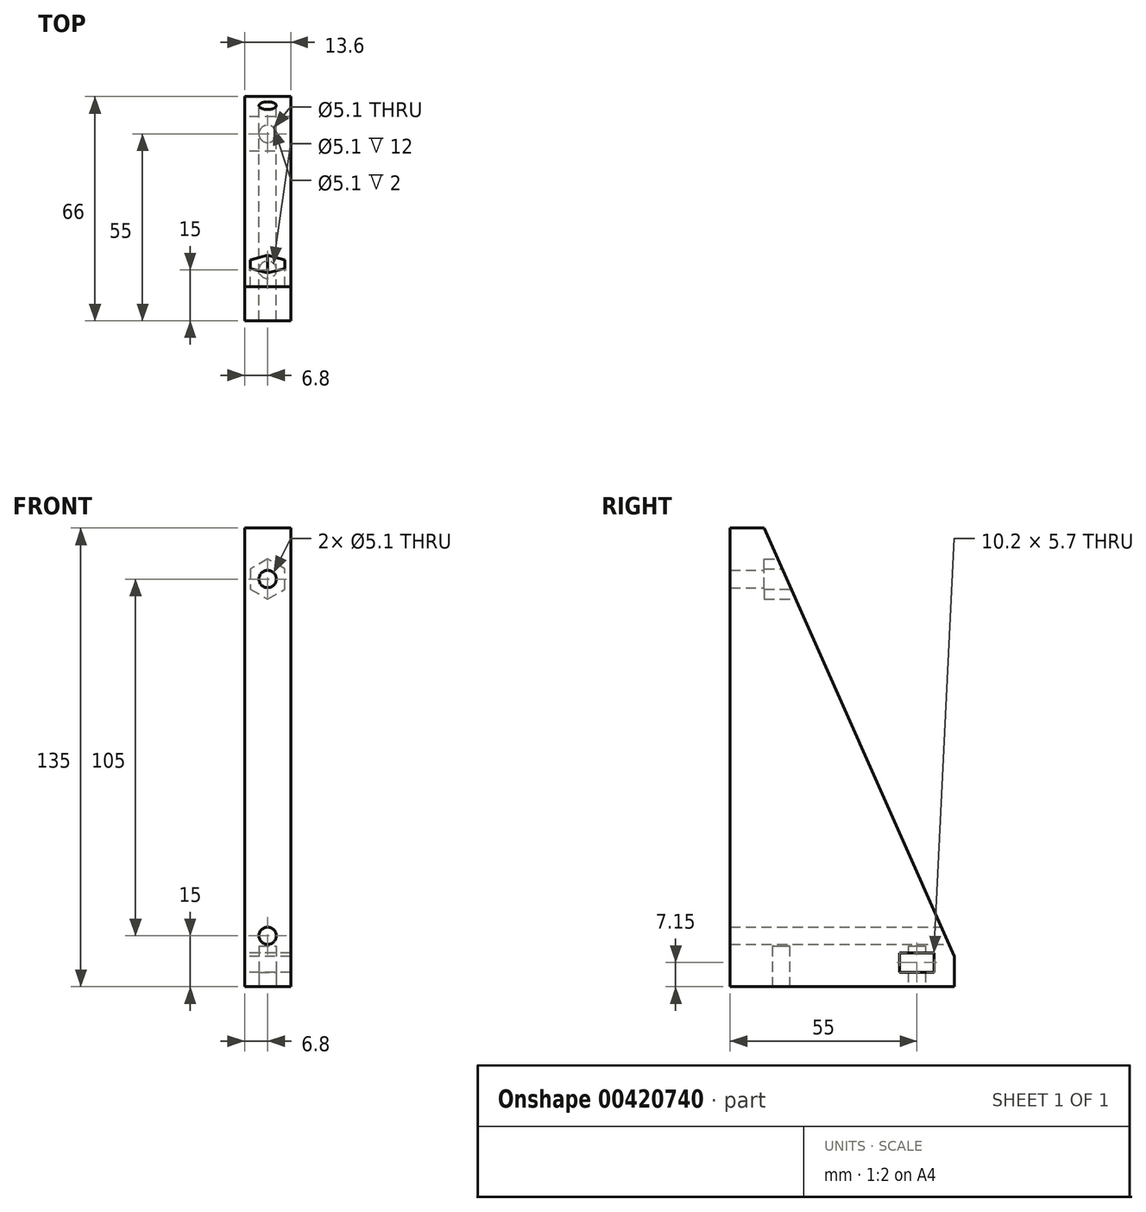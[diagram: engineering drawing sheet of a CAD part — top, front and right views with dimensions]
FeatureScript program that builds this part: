
annotation { "Feature Type Name" : "Feature", "Feature Type Description" : "" }
export const myFeature = defineFeature(function(context is Context, id is Id, definition is map)
    precondition{}
    {
        {
            var Q0;
            Q0=qCreatedBy(makeId("Right.planeOp"),FACE);
            var sketch = newSketch(context, id + "F0", { "sketchPlane" : qUnion([Q0])});
            skLineSegment(sketch, "E0", {"start": v(0, 0) * mm, "end": v(-70, 0) * mm});
            skLineSegment(sketch, "E1", {"start": v(-70, 0) * mm, "end": v(-70, 135) * mm});
            skLineSegment(sketch, "E2", {"start": v(-70, 135) * mm, "end": v(-60, 135) * mm});
            skLineSegment(sketch, "E3", {"start": v(-60, 135) * mm, "end": v(0, 0) * mm});
            skSolve(sketch);
        }
        {
            var Q0;
            Q0 = qSketchRegion(id + "F0", true);
            extrude(context, id + "F1", {"entities" : qUnion([Q0]), "depth" : 13.6 * mm});
        }
        {
            var Q0;
            Q0=makeQuery(id+"F1.opExtrude","SWEPT_FACE",FACE,{"disambiguationData":[OSD([sQuery(id+"F0.wireOp",EDGE,"E1")])]});
            var sketch = newSketch(context, id + "F2", { "sketchPlane" : qUnion([Q0])});
            skLineSegment(sketch, "E4", {"start": v(6.8, 135) * mm, "end": v(6.8, 120) * mm});
            skLineSegment(sketch, "E5", {"start": v(6.8, 0) * mm, "end": v(6.8, 15) * mm});
            skPoint(sketch, "E6.0.midPoint", {"position": v(16.6, 120) * mm});
            skCircle(sketch, "E7.cCircle", {"center": v(6.8, 15) * mm, "radius": 5.1 * mm, "construction": true});
            skLineSegment(sketch, "E7.0", {"start": v(1.7, 12.06) * mm, "end": v(1.7, 17.94) * mm});
            skLineSegment(sketch, "E7.1", {"start": v(1.7, 17.94) * mm, "end": v(6.8, 20.89) * mm});
            skLineSegment(sketch, "E7.2", {"start": v(6.8, 20.89) * mm, "end": v(11.9, 17.94) * mm});
            skLineSegment(sketch, "E7.3", {"start": v(11.9, 17.94) * mm, "end": v(11.9, 12.06) * mm});
            skLineSegment(sketch, "E7.4", {"start": v(11.9, 12.06) * mm, "end": v(6.8, 9.11) * mm});
            skLineSegment(sketch, "E7.5", {"start": v(6.8, 9.11) * mm, "end": v(1.7, 12.06) * mm});
            skPoint(sketch, "E7.0.midPoint", {"position": v(1.7, 15) * mm});
            skCircle(sketch, "E8.cCircle", {"center": v(6.8, 120) * mm, "radius": 5.1 * mm, "construction": true});
            skLineSegment(sketch, "E8.0", {"start": v(1.7, 117.06) * mm, "end": v(1.7, 122.94) * mm});
            skLineSegment(sketch, "E8.1", {"start": v(1.7, 122.94) * mm, "end": v(6.8, 125.89) * mm});
            skLineSegment(sketch, "E8.2", {"start": v(6.8, 125.89) * mm, "end": v(11.9, 122.94) * mm});
            skLineSegment(sketch, "E8.3", {"start": v(11.9, 122.94) * mm, "end": v(11.9, 117.06) * mm});
            skLineSegment(sketch, "E8.4", {"start": v(11.9, 117.06) * mm, "end": v(6.8, 114.11) * mm});
            skLineSegment(sketch, "E8.5", {"start": v(6.8, 114.11) * mm, "end": v(1.7, 117.06) * mm});
            skPoint(sketch, "E8.0.midPoint", {"position": v(1.7, 120) * mm});
            skSolve(sketch);
        }
        {
            var Q0;
            Q0=sQuery(id+"F2.wireOp",VERTEX,"E5.end");
            var Q1;
            Q1=sQuery(id+"F2.wireOp",VERTEX,"E4.end");
            var Q2;
            Q2=makeQuery(id+"F1.opExtrude","SWEPT_BODY",BODY,{"disambiguationData":[OSD([sQuery(id+"F0.wireOp",EDGE,"E0"),sQuery(id+"F0.wireOp",EDGE,"E1"),sQuery(id+"F0.wireOp",EDGE,"E2"),sQuery(id+"F0.wireOp",EDGE,"E3")])]});
            hole(context, id + "F3", {"style" : HoleStyle.SIMPLE, "endStyle" : HoleEndStyle.THROUGH, "holeDiameter" : 5.1 * mm, "isTappedThrough" : true, "tappedDepth" : 12 * mm, "tapClearance" : 3, "locations" : qUnion([Q0, Q1]), "scope" : qUnion([Q2]), "startStyle" : HoleStartStyle.PART});
        }
        {
            var Q0;
            Q0=makeQuery(id+"F1.opExtrude","SWEPT_FACE",FACE,{"disambiguationData":[OSD([sQuery(id+"F0.wireOp",EDGE,"E0")])]});
            var sketch = newSketch(context, id + "F4", { "sketchPlane" : qUnion([Q0])});
            skLineSegment(sketch, "E9", {"start": v(6.8, 70) * mm, "end": v(6.8, 55) * mm});
            skLineSegment(sketch, "E10", {"start": v(6.8, 55) * mm, "end": v(6.8, 15) * mm});
            skPoint(sketch, "E10.endSnap0", {"position": v(6.8, 0) * mm});
            skCircle(sketch, "E11", {"center": v(6.8, 55) * mm, "radius": 2.55 * mm});
            skCircle(sketch, "E12", {"center": v(6.8, 15) * mm, "radius": 2.55 * mm});
            skLineSegment(sketch, "E13", {"start": v(6.8, 0) * mm, "end": v(6.8, 4) * mm});
            skLineSegment(sketch, "E14", {"start": v(6.8, 4) * mm, "end": v(13.6, 4) * mm});
            skLineSegment(sketch, "E15", {"start": v(13.6, 4) * mm, "end": v(0, 4) * mm});
            skSolve(sketch);
        }
        {
            var Q0;
            Q0 = qSketchRegion(id + "F4", true);
            extrude(context, id + "F5", {"entities" : qUnion([Q0]), "operationType" : NewBodyOperationType.REMOVE, "oppositeDirection" : true, "depth" : 12 * mm});
        }
        {
            var Q0;
            Q0=makeQuery(id+"F2.imprint","IMPRINT",FACE,{"disambiguationData":[TD([[makeQuery(id+"F2.imprint","IMPRINT",EDGE,{"derivedFrom":sQuery(id+"F2.wireOp",EDGE,"E6.0")}),-1.0]])]});
            var Q1;
            Q1=makeQuery(id+"F2.imprint","IMPRINT",FACE,{"disambiguationData":[TD([[makeQuery(id+"F2.imprint","IMPRINT",EDGE,{"derivedFrom":sQuery(id+"F2.wireOp",EDGE,"E8.0")}),-1.0]])]});
            extrude(context, id + "F6", {"entities" : qUnion([Q0, Q1]), "operationType" : NewBodyOperationType.ADD, "oppositeDirection" : true, "depth" : 25 * mm});
        }
        {
            var Q0;
            Q0=makeQuery(id+"F6.opExtrude","CAP_FACE",FACE,{"disambiguationData":[OSD([sQuery(id+"F2.wireOp",EDGE,"E6.0"),sQuery(id+"F2.wireOp",EDGE,"E6.1"),sQuery(id+"F2.wireOp",EDGE,"E6.2"),sQuery(id+"F2.wireOp",EDGE,"E6.3"),sQuery(id+"F2.wireOp",EDGE,"E6.4"),sQuery(id+"F2.wireOp",EDGE,"E6.5")])],"isStart":false});
            var Q1;
            Q1=makeQuery(id+"F6.opExtrude","CAP_FACE",FACE,{"disambiguationData":[OSD([sQuery(id+"F2.wireOp",EDGE,"E8.0"),sQuery(id+"F2.wireOp",EDGE,"E8.1"),sQuery(id+"F2.wireOp",EDGE,"E8.2"),sQuery(id+"F2.wireOp",EDGE,"E8.3"),sQuery(id+"F2.wireOp",EDGE,"E8.4"),sQuery(id+"F2.wireOp",EDGE,"E8.5")])],"isStart":false});
            extrude(context, id + "F7", {"entities" : qUnion([Q0, Q1]), "operationType" : NewBodyOperationType.REMOVE, "oppositeDirection" : true, "depth" : 15 * mm});
        }
        {
            var Q0;
            Q0=sQuery(id+"F2.wireOp",VERTEX,"E4.end");
            var Q1;
            Q1=makeQuery(id+"F1.opExtrude","SWEPT_BODY",BODY,{"disambiguationData":[OSD([sQuery(id+"F0.wireOp",EDGE,"E0"),sQuery(id+"F0.wireOp",EDGE,"E1"),sQuery(id+"F0.wireOp",EDGE,"E2"),sQuery(id+"F0.wireOp",EDGE,"E3")])]});
            hole(context, id + "F8", {"style" : HoleStyle.SIMPLE, "endStyle" : HoleEndStyle.THROUGH, "holeDiameter" : 5.1 * mm, "isTappedThrough" : true, "tappedDepth" : 12 * mm, "tapClearance" : 3, "locations" : qUnion([Q0]), "scope" : qUnion([Q1]), "startStyle" : HoleStartStyle.PART});
        }
        {
            var Q0;
            Q0=makeQuery(id+"F1.opExtrude","CAP_FACE",FACE,{"disambiguationData":[OSD([sQuery(id+"F0.wireOp",EDGE,"E0"),sQuery(id+"F0.wireOp",EDGE,"E1"),sQuery(id+"F0.wireOp",EDGE,"E2"),sQuery(id+"F0.wireOp",EDGE,"E3")])],"isStart":true});
            var sketch = newSketch(context, id + "F9", { "sketchPlane" : qUnion([Q0])});
            skLineSegment(sketch, "E16", {"start": v(0, 0) * mm, "end": v(15, 0) * mm});
            skLineSegment(sketch, "E17", {"start": v(15, 0) * mm, "end": v(15, 10) * mm});
            skLineSegment(sketch, "E18", {"start": v(15, 10) * mm, "end": v(9.9, 10) * mm});
            skLineSegment(sketch, "E19", {"start": v(9.9, 10) * mm, "end": v(9.9, 4.3) * mm});
            skLineSegment(sketch, "E20", {"start": v(9.9, 4.3) * mm, "end": v(20.1, 4.3) * mm});
            skLineSegment(sketch, "E21", {"start": v(20.1, 4.3) * mm, "end": v(20.1, 10) * mm});
            skLineSegment(sketch, "E22", {"start": v(20.1, 10) * mm, "end": v(15, 10) * mm});
            skSolve(sketch);
        }
        {
            var Q0;
            {var subQ0=sQuery(id+"F9.wireOp",EDGE,"E18");Q0=makeQuery(id+"F9.imprint","IMPRINT",FACE,{"disambiguationData":[TD([[makeQuery(id+"F9.imprint","IMPRINT",EDGE,{"derivedFrom":subQ0}),1.0]])]});}
            var Q1;
            {var subQ4=sQuery(id+"F9.wireOp",EDGE,"E21");Q1=makeQuery(id+"F9.imprint","IMPRINT",FACE,{"disambiguationData":[TD([[makeQuery(id+"F9.imprint","IMPRINT",EDGE,{"derivedFrom":subQ4}),1.0]])]});}
            extrude(context, id + "F10", {"entities" : qUnion([Q0, Q1]), "operationType" : NewBodyOperationType.REMOVE, "oppositeDirection" : true, "depth" : 25 * mm});
        }
        {
            var Q0;
            {var subQ0=sQuery(id+"F4.wireOp",EDGE,"E13");Q0=makeQuery(id+"F4.imprint","IMPRINT",FACE,{"disambiguationData":[TD([[makeQuery(id+"F4.imprint","IMPRINT",EDGE,{"derivedFrom":subQ0}),-1.0]])]});}
            var Q1;
            {var subQ0=sQuery(id+"F4.wireOp",EDGE,"E13");Q1=makeQuery(id+"F4.imprint","IMPRINT",FACE,{"disambiguationData":[TD([[makeQuery(id+"F4.imprint","IMPRINT",EDGE,{"derivedFrom":subQ0}),1.0]])]});}
            extrude(context, id + "F11", {"entities" : qUnion([Q0, Q1]), "operationType" : NewBodyOperationType.REMOVE, "oppositeDirection" : true, "depth" : 25 * mm});
        }
    });
